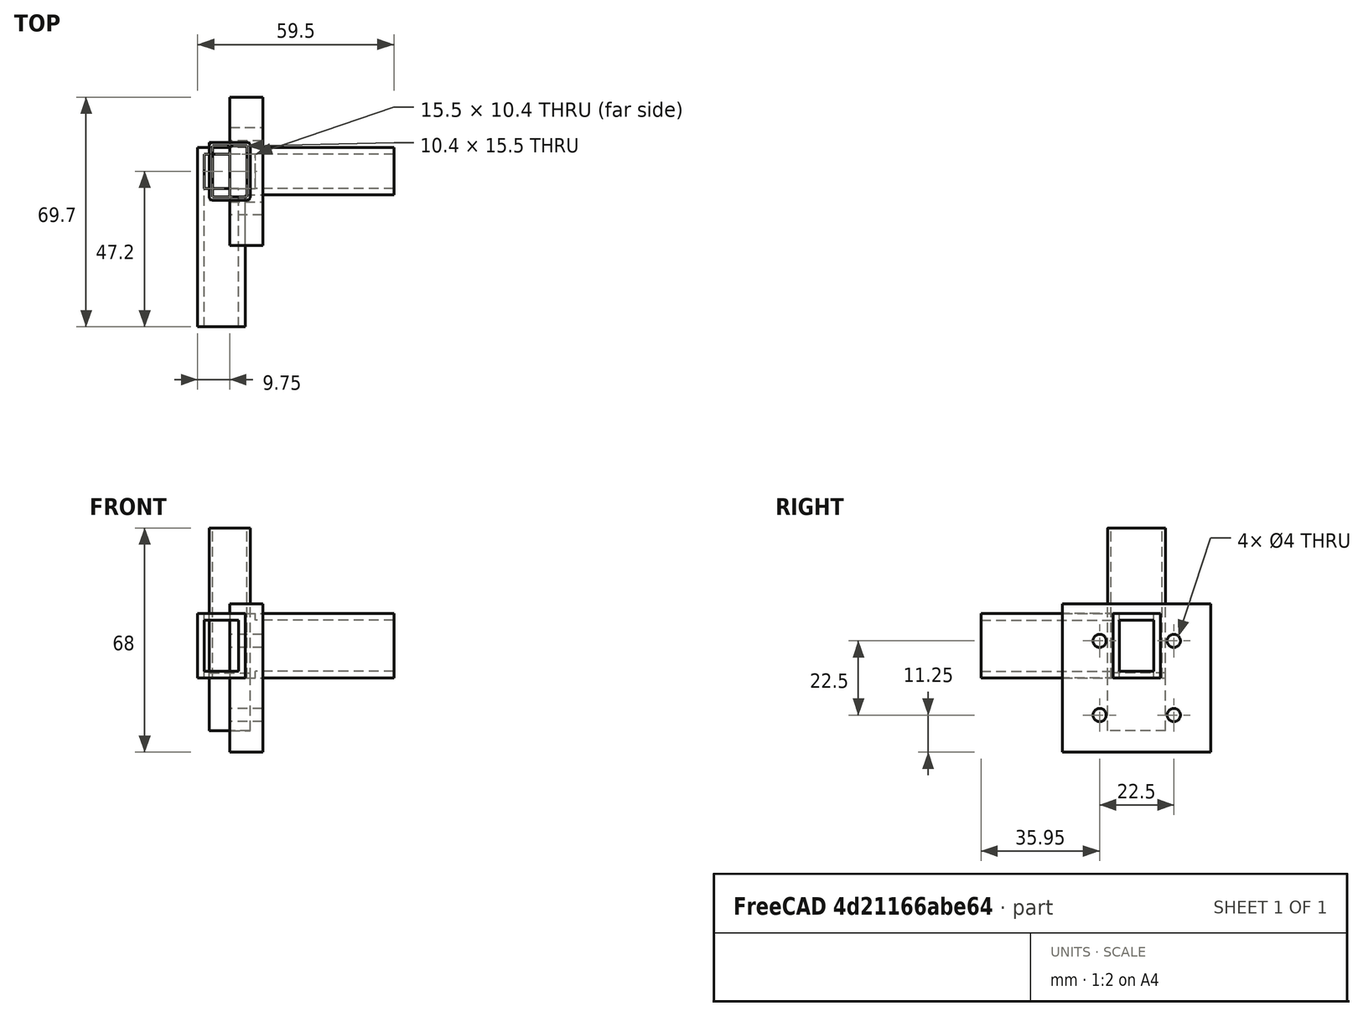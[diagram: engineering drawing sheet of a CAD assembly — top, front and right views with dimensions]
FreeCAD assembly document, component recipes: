
FREECAD ASSEMBLY — COMPONENT RECIPES ("Joints")

This assembly document has 5 components, labeled P0..P4 below (a component is one placed body or linked part). 5 of them carry a construction recipe — the FreeCAD feature program that regenerates the part from scratch, quoted from this document or its linked companion documents; the rest are supplied as boundary geometry only. No exploded tour is included for this assembly.
COMPONENT P0 — recipe-attached ("Body001", modeled in this document).
Construction recipe (the document's own serialized feature program — sketch geometry with constraints, then the solid features built on it; lengths are millimeters unless a unit is written):

FEATURE [Sketcher::SketchObject] Sketch
  AttachmentSupport = -> [XY_Plane]
  FullyConstrained = true
  MapMode = 5
  expr: Constraints[10] = Spreadsheet.width
  expr: Constraints[33] = Spreadsheet.height + Spreadsheet.thickness
  expr: Constraints[34] = Spreadsheet.width + Spreadsheet.thickness
  expr: Constraints[35] = Spreadsheet.diameter
  expr: Constraints[9] = Spreadsheet.height
  sketch-geometry (16):
    g0: LineSegment StartX=-5.2 StartY=-7.75 StartZ=0 EndX=5.2 EndY=-7.75 EndZ=0
    g1: LineSegment StartX=5.2 StartY=-7.75 StartZ=0 EndX=5.2 EndY=7.75 EndZ=0
    g2: LineSegment StartX=5.2 StartY=7.75 StartZ=0 EndX=-5.2 EndY=7.75 EndZ=0
    g3: LineSegment StartX=-5.2 StartY=7.75 StartZ=0 EndX=-5.2 EndY=-7.75 EndZ=0
    g4: GeomPoint X=0 Y=0 Z=0
    g5: LineSegment StartX=-6.2 StartY=7.75 StartZ=0 EndX=-6.2 EndY=-7.75 EndZ=0
    g6: LineSegment StartX=-5.2 StartY=-8.75 StartZ=0 EndX=5.2 EndY=-8.75 EndZ=0
    g7: LineSegment StartX=6.2 StartY=-7.75 StartZ=0 EndX=6.2 EndY=7.75 EndZ=0
    g8: LineSegment StartX=5.2 StartY=8.75 StartZ=0 EndX=-5.2 EndY=8.75 EndZ=0
    g9: ArcOfCircle CenterX=-5.2 CenterY=7.75 CenterZ=0 NormalX=0 NormalY=0 NormalZ=1 AngleXU=0 Radius=1 StartAngle=1.5708 EndAngle=3.14159
    g10: ArcOfCircle CenterX=-5.2 CenterY=-7.75 CenterZ=0 NormalX=0 NormalY=0 NormalZ=1 AngleXU=0 Radius=1 StartAngle=3.14159 EndAngle=4.71239
    g11: ArcOfCircle CenterX=5.2 CenterY=-7.75 CenterZ=0 NormalX=0 NormalY=0 NormalZ=1 AngleXU=0 Radius=1 StartAngle=4.71239 EndAngle=6.28319
    g12: ArcOfCircle CenterX=5.2 CenterY=7.75 CenterZ=0 NormalX=0 NormalY=0 NormalZ=1 AngleXU=0 Radius=1 StartAngle=2e-16 EndAngle=1.5708
    g13: GeomPoint X=-6.2 Y=8.75 Z=0
    g14: GeomPoint X=6.2 Y=-8.75 Z=0
    g15: GeomPoint X=0 Y=0 Z=0
  constraints (36):
    c: Coincident(g0,g1)
    c: Coincident(g1,g2)
    c: Coincident(g2,g3)
    c: Coincident(g3,g0)
    c: Horizontal(g0)
    c: Horizontal(g2)
    c: Vertical(g1)
    c: Vertical(g3)
    c: Symmetric(g2,g0,g4)
    c: Distance(g1,g3) = 10.4
    c: Distance(g0,g2) = 15.5
    c: Coincident(g4,g-1)
    c: Tangent(g5,g9) = -1.5708
    c: Tangent(g5,g10) = -1.5708
    c: Tangent(g6,g10) = -1.5708
    c: Tangent(g6,g11) = -1.5708
    c: Tangent(g7,g11) = -1.5708
    c: Tangent(g7,g12) = -1.5708
    c: Tangent(g8,g12) = -1.5708
    c: Tangent(g8,g9) = -1.5708
    c: Vertical(g5)
    c: Vertical(g7)
    c: Horizontal(g6)
    c: Horizontal(g8)
    c: Equal(g9,g10)
    c: Equal(g10,g11)
    c: Equal(g11,g12)
    c: PointOnObject(g13,g5)
    c: PointOnObject(g13,g8)
    c: PointOnObject(g14,g6)
    c: PointOnObject(g14,g7)
    c: Symmetric(g6,g8,g15)
    c: Coincident(g15,g4)
    c: Distance(g5,g7) = 12.4
    c: DistanceY(g6,g8) = 17.5
    c: Diameter(g12) = 2
FEATURE [PartDesign::Pad] Pad
  Direction = (0,0,1)
  Length = 45.5
  Length2 = 10
  Profile = -> Sketch
  ReferenceAxis = -> Sketch [N_Axis]
  Refine = true
  Suppressed = false
  Type = 0
  expr: Length = Spreadsheet.width + 30
FEATURE [Sketcher::SketchObject] Sketch001
  AttachmentSupport = -> [Pad]
  FullyConstrained = true
  MapMode = 5
  Placement = pos=(0,0,45.5) rot=(0,0,1;0rad)
  expr: Constraints[10] = Spreadsheet.height + Spreadsheet.thickness
  expr: Constraints[11] = Spreadsheet.width + Spreadsheet.thickness
  sketch-geometry (5):
    g0: LineSegment StartX=-6.2 StartY=8.75 StartZ=0 EndX=-6.2 EndY=-8.75 EndZ=0
    g1: LineSegment StartX=-6.2 StartY=-8.75 StartZ=0 EndX=6.2 EndY=-8.75 EndZ=0
    g2: LineSegment StartX=6.2 StartY=-8.75 StartZ=0 EndX=6.2 EndY=8.75 EndZ=0
    g3: LineSegment StartX=6.2 StartY=8.75 StartZ=0 EndX=-6.2 EndY=8.75 EndZ=0
    g4: GeomPoint X=0 Y=0 Z=0
  constraints (12):
    c: Coincident(g0,g1)
    c: Coincident(g1,g2)
    c: Coincident(g2,g3)
    c: Coincident(g3,g0)
    c: Vertical(g0)
    c: Vertical(g2)
    c: Horizontal(g1)
    c: Horizontal(g3)
    c: Symmetric(g2,g0,g4)
    c: Coincident(g4,g-1)
    c: Distance(g3,g3) = 12.4
    c: DistanceY(g2,g2) = 17.5
FEATURE [PartDesign::Body] Body
  Group = -> [Sketch,Pad,Sketch001]
  Origin = -> Origin
  Tip = -> Pad
COMPONENT P1 — same part as P0; its construction recipe is shown at P0.
COMPONENT P2 — same part as P0; its construction recipe is shown at P0.
COMPONENT P3 — recipe-attached ("Body005", modeled in this document).
Construction recipe (the document's own serialized feature program — sketch geometry with constraints, then the solid features built on it; lengths are millimeters unless a unit is written):

FEATURE [Sketcher::SketchObject] Sketch002
  AttachmentSupport = -> [XY_Plane002]
  FullyConstrained = true
  MapMode = 5
  expr: Constraints[10] = Spreadsheet.height + Spreadsheet.thickness
  expr: Constraints[11] = Spreadsheet.width + Spreadsheet.thickness
  sketch-geometry (5):
    g0: LineSegment StartX=-6.2 StartY=8.75 StartZ=0 EndX=-6.2 EndY=-8.75 EndZ=0
    g1: LineSegment StartX=-6.2 StartY=-8.75 StartZ=0 EndX=6.2 EndY=-8.75 EndZ=0
    g2: LineSegment StartX=6.2 StartY=-8.75 StartZ=0 EndX=6.2 EndY=8.75 EndZ=0
    g3: LineSegment StartX=6.2 StartY=8.75 StartZ=0 EndX=-6.2 EndY=8.75 EndZ=0
    g4: GeomPoint X=0 Y=0 Z=0
  constraints (12):
    c: Coincident(g0,g1)
    c: Coincident(g1,g2)
    c: Coincident(g2,g3)
    c: Coincident(g3,g0)
    c: Vertical(g0)
    c: Vertical(g2)
    c: Horizontal(g1)
    c: Horizontal(g3)
    c: Symmetric(g2,g0,g4)
    c: Coincident(g4,g-1)
    c: Distance(g3,g3) = 12.4
    c: DistanceY(g2,g2) = 17.5
FEATURE [PartDesign::Pad] Pad001
  Direction = (0,0,1)
  Length = 17.5
  Length2 = 10
  Profile = -> Sketch002
  ReferenceAxis = -> Sketch002 [N_Axis]
  Refine = true
  Suppressed = false
  Type = 0
  expr: Length = Spreadsheet.thickness + Spreadsheet.width
FEATURE [PartDesign::Body] Body004
  Group = -> [Sketch002,Pad001]
  Origin = -> Origin002
  Placement = pos=(0,0,-16) rot=(0,0,1;0rad)
  Tip = -> Pad001
COMPONENT P4 — recipe-attached ("Body007", modeled in this document).
Construction recipe (the document's own serialized feature program — sketch geometry with constraints, then the solid features built on it; lengths are millimeters unless a unit is written):

FEATURE [Sketcher::SketchObject] Sketch003
  AttachmentSupport = -> [YZ_Plane003]
  FullyConstrained = true
  MapMode = 5
  Placement = pos=(0,0,0) rot=(0.57735,0.57735,0.57735;2.0944rad)
  sketch-geometry (10):
    g0: LineSegment StartX=-22.5 StartY=-22.5 StartZ=0 EndX=22.5 EndY=-22.5 EndZ=0
    g1: LineSegment StartX=22.5 StartY=-22.5 StartZ=0 EndX=22.5 EndY=22.5 EndZ=0
    g2: LineSegment StartX=22.5 StartY=22.5 StartZ=0 EndX=-22.5 EndY=22.5 EndZ=0
    g3: LineSegment StartX=-22.5 StartY=22.5 StartZ=0 EndX=-22.5 EndY=-22.5 EndZ=0
    g4: GeomPoint X=0 Y=0 Z=0
    g5: Circle CenterX=-11.25 CenterY=-11.25 CenterZ=0 NormalX=0 NormalY=0 NormalZ=1 AngleXU=0 Radius=2
    g6: Circle CenterX=11.25 CenterY=-11.25 CenterZ=0 NormalX=0 NormalY=0 NormalZ=1 AngleXU=0 Radius=2
    g7: Circle CenterX=11.25 CenterY=11.25 CenterZ=0 NormalX=0 NormalY=0 NormalZ=1 AngleXU=0 Radius=2
    g8: Circle CenterX=-11.25 CenterY=11.25 CenterZ=0 NormalX=0 NormalY=0 NormalZ=1 AngleXU=0 Radius=2
    g9: GeomPoint X=0 Y=0 Z=0
  constraints (23):
    c: Coincident(g0,g1)
    c: Coincident(g1,g2)
    c: Coincident(g2,g3)
    c: Coincident(g3,g0)
    c: Horizontal(g0)
    c: Horizontal(g2)
    c: Vertical(g1)
    c: Vertical(g3)
    c: Symmetric(g2,g0,g4)
    c: Distance(g1,g3) = 45
    c: Distance(g0,g2) = 45
    c: Coincident(g4,g-1)
    c: Equal(g8,g7)
    c: Equal(g7,g6)
    c: Equal(g6,g5)
    c: Horizontal(g8,g7)
    c: Horizontal(g5,g6)
    c: Vertical(g8,g5)
    c: Vertical(g7,g6)
    c: Symmetric(g5,g7,g9)
    c: Coincident(g9,g4)
    c: Diameter(g7) = 4
    c: Symmetric(g4,g1,g7)
FEATURE [PartDesign::Pad] Pad002
  Direction = (1,0,0)
  Length = 10
  Length2 = 10
  Placement = pos=(0,0,0) rot=(1,1,1;2.0944rad)
  Profile = -> Sketch003
  ReferenceAxis = -> Sketch003 [N_Axis]
  Refine = true
  Suppressed = false
  Type = 0
  expr: Length = 10 mm
FEATURE [PartDesign::Body] Body006
  Group = -> [Sketch003,Pad002]
  Origin = -> Origin003
  Tip = -> Pad002
PROVENANCE & LICENSES
A FreeCAD (.FCStd) document from a public repository crawl; recipes are the document's own serialized feature recipes (and, for linked parts, companion documents' recipes).
License: as declared in the source repository (recorded in the dataset sidecar).
